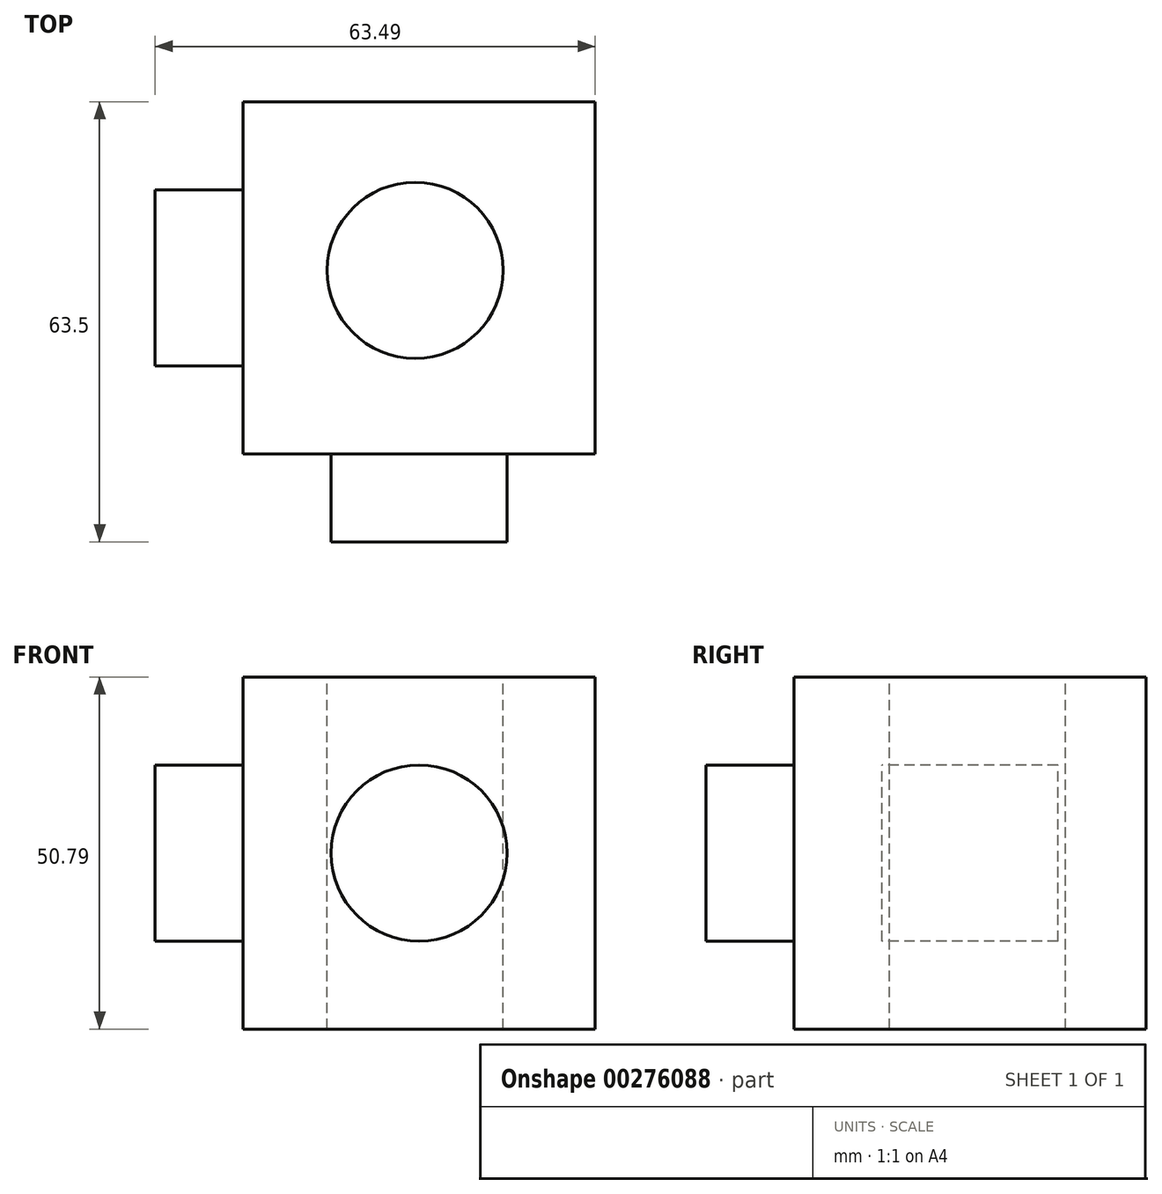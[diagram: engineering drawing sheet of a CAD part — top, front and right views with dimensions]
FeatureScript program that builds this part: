
annotation { "Feature Type Name" : "Feature", "Feature Type Description" : "" }
export const myFeature = defineFeature(function(context is Context, id is Id, definition is map)
    precondition{}
    {
        {
            var Q0;
            Q0=qCreatedBy(makeId("Front.planeOp"),FACE);
            var sketch = newSketch(context, id + "F0", { "sketchPlane" : qUnion([Q0])});
            skLineSegment(sketch, "E0.bottom", {"start": v(0, 0) * mm, "end": v(-50.8, 0) * mm});
            skLineSegment(sketch, "E0.top", {"start": v(0, 50.8) * mm, "end": v(-50.8, 50.8) * mm});
            skLineSegment(sketch, "E0.left", {"start": v(0, 0) * mm, "end": v(0, 50.8) * mm});
            skLineSegment(sketch, "E0.right", {"start": v(-50.8, 0) * mm, "end": v(-50.8, 50.8) * mm});
            skSolve(sketch);
        }
        {
            var Q0;
            Q0=makeQuery(id+"F0.imprint","IMPRINT",FACE,{"disambiguationData":[TD([[makeQuery(id+"F0.imprint","IMPRINT",EDGE,{"derivedFrom":sQuery(id+"F0.wireOp",EDGE,"E0.bottom")}),-1.0]])]});
            extrude(context, id + "F1", {"entities" : qUnion([Q0]), "depth" : 50.8 * mm});
        }
        {
            var Q0;
            Q0=makeQuery(id+"F1.opExtrude","SWEPT_FACE",FACE,{"disambiguationData":[OSD([sQuery(id+"F0.wireOp",EDGE,"E0.top")])]});
            var sketch = newSketch(context, id + "F2", { "sketchPlane" : qUnion([Q0])});
            skCircle(sketch, "E1", {"center": v(-25.97, -24.33) * mm, "radius": 12.7 * mm});
            skSolve(sketch);
        }
        {
            var Q0;
            Q0 = qSketchRegion(id + "F2", true);
            extrude(context, id + "F3", {"entities" : qUnion([Q0]), "operationType" : NewBodyOperationType.REMOVE, "oppositeDirection" : true, "depth" : 50.8 * mm});
        }
        {
            var Q0;
            Q0=makeQuery(id+"F1.opExtrude","SWEPT_FACE",FACE,{"disambiguationData":[OSD([sQuery(id+"F0.wireOp",EDGE,"E0.right")])]});
            var sketch = newSketch(context, id + "F4", { "sketchPlane" : qUnion([Q0])});
            skLineSegment(sketch, "E2.bottom", {"start": v(12.7, 12.7) * mm, "end": v(38.1, 12.7) * mm});
            skLineSegment(sketch, "E2.top", {"start": v(12.7, 38.1) * mm, "end": v(38.1, 38.1) * mm});
            skLineSegment(sketch, "E2.left", {"start": v(12.7, 12.7) * mm, "end": v(12.7, 38.1) * mm});
            skLineSegment(sketch, "E2.right", {"start": v(38.1, 12.7) * mm, "end": v(38.1, 38.1) * mm});
            skSolve(sketch);
        }
        {
            var Q0;
            Q0=makeQuery(id+"F4.imprint","IMPRINT",FACE,{"disambiguationData":[TD([[makeQuery(id+"F4.imprint","IMPRINT",EDGE,{"derivedFrom":sQuery(id+"F4.wireOp",EDGE,"E2.bottom")}),1.0]])]});
            extrude(context, id + "F5", {"entities" : qUnion([Q0]), "operationType" : NewBodyOperationType.ADD, "depth" : 12.7 * mm});
        }
        {
            var Q0;
            Q0=makeQuery(id+"F1.opExtrude","CAP_FACE",FACE,{"disambiguationData":[OSD([sQuery(id+"F0.wireOp",EDGE,"E0.bottom"),sQuery(id+"F0.wireOp",EDGE,"E0.top"),sQuery(id+"F0.wireOp",EDGE,"E0.left"),sQuery(id+"F0.wireOp",EDGE,"E0.right")])],"isStart":false});
            var sketch = newSketch(context, id + "F6", { "sketchPlane" : qUnion([Q0])});
            skCircle(sketch, "E3", {"center": v(-25.4, 25.4) * mm, "radius": 12.7 * mm});
            skSolve(sketch);
        }
        {
            var Q0;
            Q0=makeQuery(id+"F6.imprint","IMPRINT",FACE,{"disambiguationData":[TD([[makeQuery(id+"F6.imprint","IMPRINT",EDGE,{"derivedFrom":sQuery(id+"F6.wireOp",EDGE,"E3")}),1.0]])]});
            extrude(context, id + "F7", {"entities" : qUnion([Q0]), "operationType" : NewBodyOperationType.ADD, "depth" : 12.7 * mm});
        }
    });
